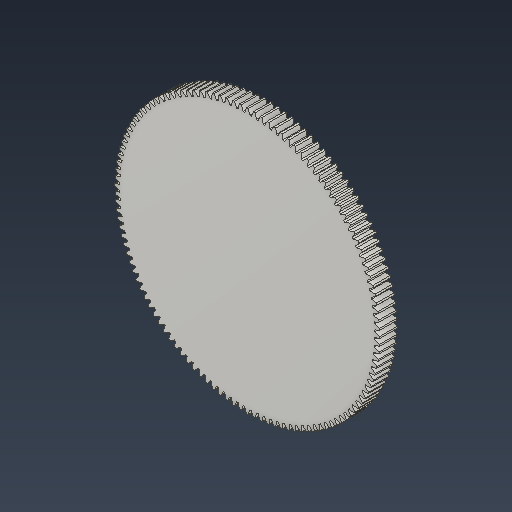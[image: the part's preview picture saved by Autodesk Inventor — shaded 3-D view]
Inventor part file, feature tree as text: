
AUTODESK INVENTOR PART (.ipt)
format: ipt  version: 2022 (Build 260153000, 153)  size: 617,984 bytes
history: native  units: mm (DEFAULTED — no unit token found)
features: plane x3, other x3, sketch x2, extrude x1
ambient origin geometry x8: Origin, YZ Plane, XZ Plane, XY Plane, X Axis, Y Axis, Z Axis, Center Point
bodies: Solid1 (feature_tree)
feature tree (9):
  extrude  "Extrusion1"  Depth=20.0mm TaperAngle=0.0deg
  plane  "Work Plane2"
  plane  "Work Plane8"
  plane  "Work Plane9"
  other  "Spur Gear"
  sketch  "Sketch1"  dims[d0=305.0mm d1=20.0mm d2=0.0mm]
  sketch  "Sketch2"  dims[d3=300.0mm d4=10.0mm d5=0.0mm d16=300.0mm d17=0.0mm d34=0.261799mm d39=0.0mm d41=0.0mm d43=300.0mm d46=300.0mm d47=0.0mm d48=0.0mm]
  other  "Srf1"
  other  "Pitch Diameter"
